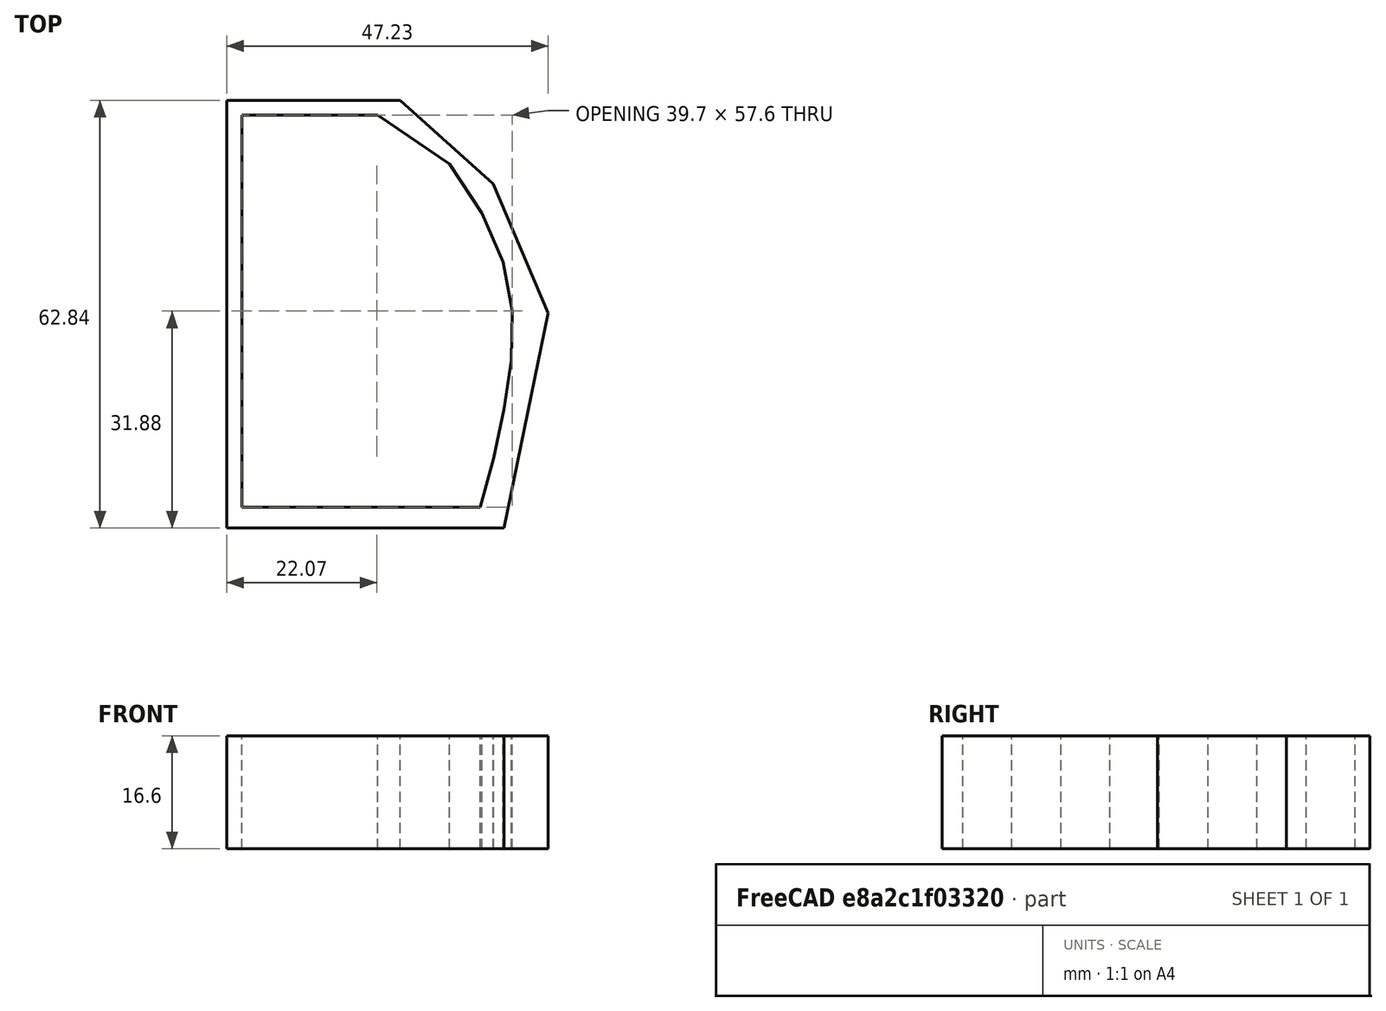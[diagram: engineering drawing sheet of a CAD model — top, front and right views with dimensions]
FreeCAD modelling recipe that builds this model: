
FCSTD DOCUMENT  (FreeCAD 0.19R24291 (Git))
Label: side-walls
License: All rights reserved
LicenseURL: http://en.wikipedia.org/wiki/All_rights_reserved
objects: Sketcher::SketchObject×1, PartDesign::Pad×1, PartDesign::Body×1
note: 4 computed .brp shape members not serialized (recipe doc carries the construction recipe); baked Part::Feature solids carry a one-line shape summary decoded from their .brp

FEATURE [Sketcher::SketchObject] Sketch
  FullyConstrained = false
  MapMode = 5
  Support = -> [XY_Plane]
  sketch-geometry (17):
    g0: LineSegment StartX=0 StartY=0 StartZ=0 EndX=35 EndY=0 EndZ=0
    g1: LineSegment StartX=35 StartY=0 StartZ=0 EndX=37 EndY=7.2 EndZ=0
    g2: LineSegment StartX=37 StartY=7.2 StartZ=0 EndX=38.5 EndY=14.4 EndZ=0
    g3: LineSegment StartX=38.5 StartY=14.4 StartZ=0 EndX=39.6 EndY=21.6 EndZ=0
    g4: LineSegment StartX=39.6 StartY=21.6 StartZ=0 EndX=39.7 EndY=28.8 EndZ=0
    g5: LineSegment StartX=39.7 StartY=28.8 StartZ=0 EndX=38.4 EndY=36 EndZ=0
    g6: LineSegment StartX=38.4 StartY=36 StartZ=0 EndX=35.3 EndY=43.2 EndZ=0
    g7: LineSegment StartX=35.3 StartY=43.2 StartZ=0 EndX=30.5 EndY=50.4 EndZ=0
    g8: LineSegment StartX=30.5 StartY=50.4 StartZ=0 EndX=20 EndY=57.6 EndZ=0
    g9: LineSegment StartX=20 StartY=57.6 StartZ=0 EndX=0 EndY=57.6 EndZ=0
    g10: LineSegment StartX=0 StartY=57.6 StartZ=0 EndX=0 EndY=0 EndZ=0
    g11: LineSegment StartX=-2.21516 StartY=59.7598 StartZ=0 EndX=-2.21516 EndY=-3.07541 EndZ=0
    g12: LineSegment StartX=-2.21516 StartY=-3.07541 StartZ=0 EndX=38.4894 EndY=-3.07541 EndZ=0
    g13: LineSegment StartX=38.4894 StartY=-3.07541 StartZ=0 EndX=45.01 EndY=28.5398 EndZ=0
    g14: LineSegment StartX=45.01 StartY=28.5398 StartZ=0 EndX=36.9087 EndY=47.5089 EndZ=0
    g15: LineSegment StartX=36.9087 StartY=47.5089 StartZ=0 EndX=23.2746 EndY=59.7598 EndZ=0
    g16: LineSegment StartX=23.2746 StartY=59.7598 StartZ=0 EndX=-2.21516 EndY=59.7598 EndZ=0
  constraints (41):
    c: Coincident(g-1,g0)
    c: PointOnObject(g0,g-1)
    c: Coincident(g0,g1)
    c: Coincident(g1,g2)
    c: Coincident(g2,g3)
    c: Coincident(g3,g4)
    c: Coincident(g4,g5)
    c: Coincident(g5,g6)
    c: Coincident(g6,g7)
    c: Coincident(g7,g8)
    c: Coincident(g8,g9)
    c: PointOnObject(g9,g-2)
    c: Horizontal(g9)
    c: Coincident(g9,g10)
    c: Coincident(g10,g0)
    c: DistanceX(g0,g1) = 37
    c: DistanceX(g0,g2) = 38.5
    c: DistanceX(g0,g3) = 39.6
    c: DistanceX(g0,g4) = 39.7
    c: DistanceX(g0,g5) = 38.4
    c: DistanceX(g0,g6) = 35.3
    c: DistanceX(g0,g7) = 30.5
    c: DistanceX(g0,g8) = 20
    c: DistanceX(g0,g0) = 35
    c: DistanceY(g7,g8) = 7.2
    c: DistanceY(g6,g7) = 7.2
    c: DistanceY(g5,g6) = 7.2
    c: DistanceY(g4,g5) = 7.2
    c: DistanceY(g3,g4) = 7.2
    c: DistanceY(g2,g3) = 7.2
    c: DistanceY(g1,g2) = 7.2
    c: DistanceY(g0,g1) = 7.2
    c: Vertical(g11)
    c: Coincident(g11,g12)
    c: Horizontal(g12)
    c: Coincident(g12,g13)
    c: Coincident(g13,g14)
    c: Coincident(g14,g15)
    c: Coincident(g15,g16)
    c: Coincident(g16,g11)
    c: Horizontal(g16)
FEATURE [PartDesign::Pad] Pad
  Direction = (1,1,1)
  Length = 16.6
  Length2 = 100
  Profile = -> Sketch
  Type = 0
FEATURE [PartDesign::Body] Body
  Group = -> [Sketch,Pad]
  Origin = -> Origin
  Tip = -> Pad
